# Revit family: Faucet-CA-Grohe-Eurosmart-20294XX3_Series
name_source: partatom
category: Plumbing Fixtures
revit_build: Autodesk Revit 2018 (Build: 20170223_1515(x64)
units: mm (PartAtom-declared; Revit-internal decimal feet)

## family parameters
Always vertical = No
Cut with Voids When Loaded = No
OmniClass Number = 23.45.55.17
OmniClass Title = Mixing Faucets
Part Type = Normal
Room Calculation Point = No
Round Connector Dimension = Use Diameter
Shared = Yes
Work Plane-Based = Yes

## types (2) — shared parameters
ADA Compliant = Yes
Assembly Code = D2020300
CW Connection = Yes
CWFU = 1.5
Cold Water Connection Diameter = 1/2"
Default Elevation = 0"
Description = The Eurosmart 8” Widespread Bathroom Faucet from GROHE has a contemporary design engineered to the exacting standards you expect from GROHE. The strong lines of its cylindrical base are complemented by gently curved, ergonomic handles. The perfectly angled aerator creates a unique outward water flow. These design details result in a highly comfortable user experience. Exclusive GROHE features, including water-saving GROHE EcoJoy, make the Eurosmart faucet an essential addition to today’s home.
Distance between Handles = 8"
Distance between Handles Constraint = 8"
Flow Rate = 4.5 L/MIN (1.2 GPM)
HW Connection = Yes
HWFU = 1.5
Height = 5 1/16"
Hot Water Connection Diameter = 1/2"
IAPMO Compliance = • ADA • WaterSense • CEC Certified • Low Lead Certified • CALGreen Compliant • Massachusetts Plumbing Board Approved • Energy Policy Act of 1992 • NSF 61 • NSF 372 • CSA B125.1 • ASME A112.18.1 • Complies with lead plumbing laws
Length = 5 7/8"
Manufacturer = Grohe
Price = Prices may vary. Please consult Manufacturer Representative for most up-to-date price list.
URL = https://www.grohe.ca
Vent Connection = No
WFU = 2
Waste Connection = No
Width = 17 11/16"

## per-type parameters (varying)
| type | Finish | Material | Product Documentation Link | Product Page URL |
| 20294003 | Metal-Grohe-StarLight Chrome | Metal-Grohe-StarLight Chrome |  |  |
| 20294EN3 | Metal-Grohe-Brushed Nickel Infinity | Metal-Grohe-Brushed Nickel Infinity | https://americanstandard.box.com | https://www.grohe.ca |

note: column(s) folded — value = type name in every type: Model

## geometry (parser evidence)
native form markers: Sweep x2
no freeform markers — native parametric forms only
